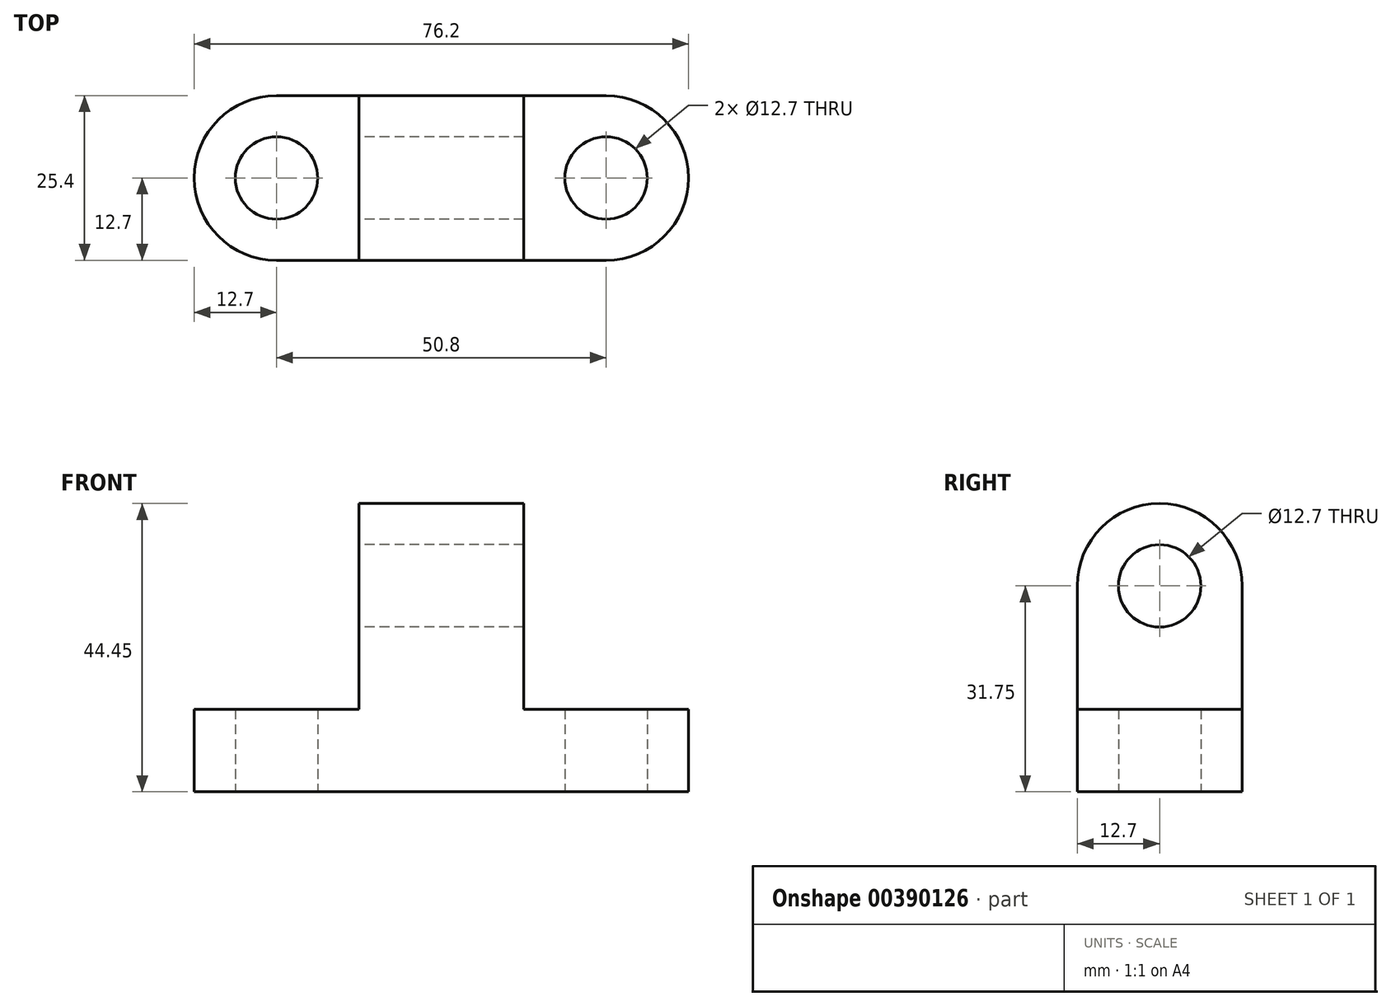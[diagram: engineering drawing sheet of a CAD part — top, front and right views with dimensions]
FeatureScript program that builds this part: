
annotation { "Feature Type Name" : "Feature", "Feature Type Description" : "" }
export const myFeature = defineFeature(function(context is Context, id is Id, definition is map)
    precondition{}
    {
        {
            var Q0;
            Q0=qCreatedBy(makeId("Front.planeOp"),FACE);
            var sketch = newSketch(context, id + "F0", { "sketchPlane" : qUnion([Q0])});
            skLineSegment(sketch, "E0", {"start": v(0, 0) * mm, "end": v(76.2, 0) * mm});
            skLineSegment(sketch, "E1", {"start": v(76.2, 0) * mm, "end": v(76.2, 12.7) * mm});
            skLineSegment(sketch, "E2", {"start": v(76.2, 12.7) * mm, "end": v(50.8, 12.7) * mm});
            skLineSegment(sketch, "E3", {"start": v(50.8, 12.7) * mm, "end": v(50.8, 44.45) * mm});
            skLineSegment(sketch, "E4", {"start": v(50.8, 44.45) * mm, "end": v(25.4, 44.45) * mm});
            skLineSegment(sketch, "E5", {"start": v(25.4, 44.45) * mm, "end": v(25.4, 12.7) * mm});
            skLineSegment(sketch, "E6", {"start": v(25.4, 12.7) * mm, "end": v(0, 12.7) * mm});
            skLineSegment(sketch, "E7", {"start": v(0, 12.7) * mm, "end": v(0, 0) * mm});
            skSolve(sketch);
        }
        {
            var Q0;
            Q0=makeQuery(id+"F0.imprint","IMPRINT",FACE,{"disambiguationData":[TD([[makeQuery(id+"F0.imprint","IMPRINT",EDGE,{"derivedFrom":sQuery(id+"F0.wireOp",EDGE,"E0")}),1.0]])]});
            extrude(context, id + "F1", {"entities" : qUnion([Q0]), "depth" : 25.4 * mm});
        }
        {
            var Q0;
            Q0=qCreatedBy(makeId("Right.planeOp"),FACE);
            var sketch = newSketch(context, id + "F2", { "sketchPlane" : qUnion([Q0])});
            skCircle(sketch, "E8", {"center": v(-12.7, 31.75) * mm, "radius": 6.35 * mm});
            skArc(sketch, "E9", {"start": v(0, 31.75) * mm, "mid": v(-12.7, 44.45) * mm, "end": v(-25.4, 31.75) * mm});
            skLineSegment(sketch, "E10", {"start": v(0, 31.75) * mm, "end": v(0, 44.45) * mm});
            skPoint(sketch, "E10.endSnap0", {"position": v(-12.7, 44.45) * mm});
            skLineSegment(sketch, "E11", {"start": v(0, 44.45) * mm, "end": v(-25.4, 44.45) * mm});
            skLineSegment(sketch, "E12", {"start": v(-25.4, 44.45) * mm, "end": v(-25.4, 31.75) * mm});
            skSolve(sketch);
        }
        {
            var Q0;
            Q0=makeQuery(id+"F2.imprint","IMPRINT",FACE,{"disambiguationData":[TD([[makeQuery(id+"F2.imprint","IMPRINT",EDGE,{"derivedFrom":sQuery(id+"F2.wireOp",EDGE,"E8")}),1.0]])]});
            var Q1;
            {var subQ0=sQuery(id+"F2.wireOp",EDGE,"mh2HlcRG-xzYn-i8Fo-nZnj-zS9WSP3q8JPp");Q1=makeQuery(id+"F2.imprint","IMPRINT",FACE,{"disambiguationData":[TD([[makeQuery(id+"F2.imprint","IMPRINT",EDGE,{"derivedFrom":subQ0}),-1.0]])]});}
            var Q2;
            {var subQ0=sQuery(id+"F2.wireOp",EDGE,"E12");Q2=makeQuery(id+"F2.imprint","IMPRINT",FACE,{"disambiguationData":[TD([[makeQuery(id+"F2.imprint","IMPRINT",EDGE,{"derivedFrom":subQ0}),1.0]])]});}
            var Q3;
            {var subQ0=sQuery(id+"F2.wireOp",EDGE,"E10");Q3=makeQuery(id+"F2.imprint","IMPRINT",FACE,{"disambiguationData":[TD([[makeQuery(id+"F2.imprint","IMPRINT",EDGE,{"derivedFrom":subQ0}),1.0]])]});}
            extrude(context, id + "F3", {"entities" : qUnion([Q0, Q1, Q2, Q3]), "operationType" : NewBodyOperationType.REMOVE, "depth" : 76.2 * mm});
        }
        {
            var Q0;
            Q0=qCreatedBy(makeId("Top.planeOp"),FACE);
            var sketch = newSketch(context, id + "F4", { "sketchPlane" : qUnion([Q0])});
            skCircle(sketch, "E13", {"center": v(63.5, -12.7) * mm, "radius": 6.35 * mm});
            skCircle(sketch, "E14", {"center": v(12.7, -12.7) * mm, "radius": 6.35 * mm});
            skArc(sketch, "E15", {"start": v(12.7, 0) * mm, "mid": v(0, -12.7) * mm, "end": v(12.7, -25.4) * mm});
            skLineSegment(sketch, "E16", {"start": v(12.7, -25.4) * mm, "end": v(0, -25.4) * mm});
            skLineSegment(sketch, "E17", {"start": v(0, 0) * mm, "end": v(12.7, 0) * mm});
            skLineSegment(sketch, "E18", {"start": v(0, 0) * mm, "end": v(0, -25.4) * mm});
            skArc(sketch, "E19", {"start": v(63.5, -25.4) * mm, "mid": v(76.2, -12.7) * mm, "end": v(63.5, 0) * mm});
            skLineSegment(sketch, "E20", {"start": v(63.5, -25.4) * mm, "end": v(76.2, -25.4) * mm});
            skLineSegment(sketch, "E21", {"start": v(76.2, -25.4) * mm, "end": v(76.2, 0) * mm});
            skLineSegment(sketch, "E22", {"start": v(76.2, 0) * mm, "end": v(63.5, 0) * mm});
            skSolve(sketch);
        }
        {
            var Q0;
            Q0=makeQuery(id+"F4.imprint","IMPRINT",FACE,{"disambiguationData":[TD([[makeQuery(id+"F4.imprint","IMPRINT",EDGE,{"derivedFrom":sQuery(id+"F4.wireOp",EDGE,"E13")}),1.0]])]});
            var Q1;
            {var subQ0=sQuery(id+"F4.wireOp",EDGE,"xwbsOgWO-vhqp-iXBC-nNxS-nkW1fuO8q3xX");Q1=makeQuery(id+"F4.imprint","IMPRINT",FACE,{"disambiguationData":[TD([[makeQuery(id+"F4.imprint","IMPRINT",EDGE,{"derivedFrom":subQ0}),-1.0]])]});}
            var Q2;
            {var subQ0=sQuery(id+"F4.wireOp",EDGE,"DyyJXNme-EZ4d-fogD-lLUb-7PGKHH0AFZhv");Q2=makeQuery(id+"F4.imprint","IMPRINT",FACE,{"disambiguationData":[TD([[makeQuery(id+"F4.imprint","IMPRINT",EDGE,{"derivedFrom":subQ0}),-1.0]])]});}
            var Q3;
            {var subQ0=sQuery(id+"F4.wireOp",EDGE,"E16");Q3=makeQuery(id+"F4.imprint","IMPRINT",FACE,{"disambiguationData":[TD([[makeQuery(id+"F4.imprint","IMPRINT",EDGE,{"derivedFrom":subQ0}),-1.0]])]});}
            var Q4;
            {var subQ0=sQuery(id+"F4.wireOp",EDGE,"E17");Q4=makeQuery(id+"F4.imprint","IMPRINT",FACE,{"disambiguationData":[TD([[makeQuery(id+"F4.imprint","IMPRINT",EDGE,{"derivedFrom":subQ0}),-1.0]])]});}
            var Q5;
            Q5=makeQuery(id+"F4.imprint","IMPRINT",FACE,{"disambiguationData":[TD([[makeQuery(id+"F4.imprint","IMPRINT",EDGE,{"derivedFrom":sQuery(id+"F4.wireOp",EDGE,"E14")}),1.0]])]});
            var Q6;
            {var subQ0=sQuery(id+"F4.wireOp",EDGE,"E20");Q6=makeQuery(id+"F4.imprint","IMPRINT",FACE,{"disambiguationData":[TD([[makeQuery(id+"F4.imprint","IMPRINT",EDGE,{"derivedFrom":subQ0}),1.0]])]});}
            var Q7;
            {var subQ0=sQuery(id+"F4.wireOp",EDGE,"E22");Q7=makeQuery(id+"F4.imprint","IMPRINT",FACE,{"disambiguationData":[TD([[makeQuery(id+"F4.imprint","IMPRINT",EDGE,{"derivedFrom":subQ0}),1.0]])]});}
            extrude(context, id + "F5", {"entities" : qUnion([Q0, Q1, Q2, Q3, Q4, Q5, Q6, Q7]), "operationType" : NewBodyOperationType.REMOVE, "depth" : 12.7 * mm});
        }
    });
